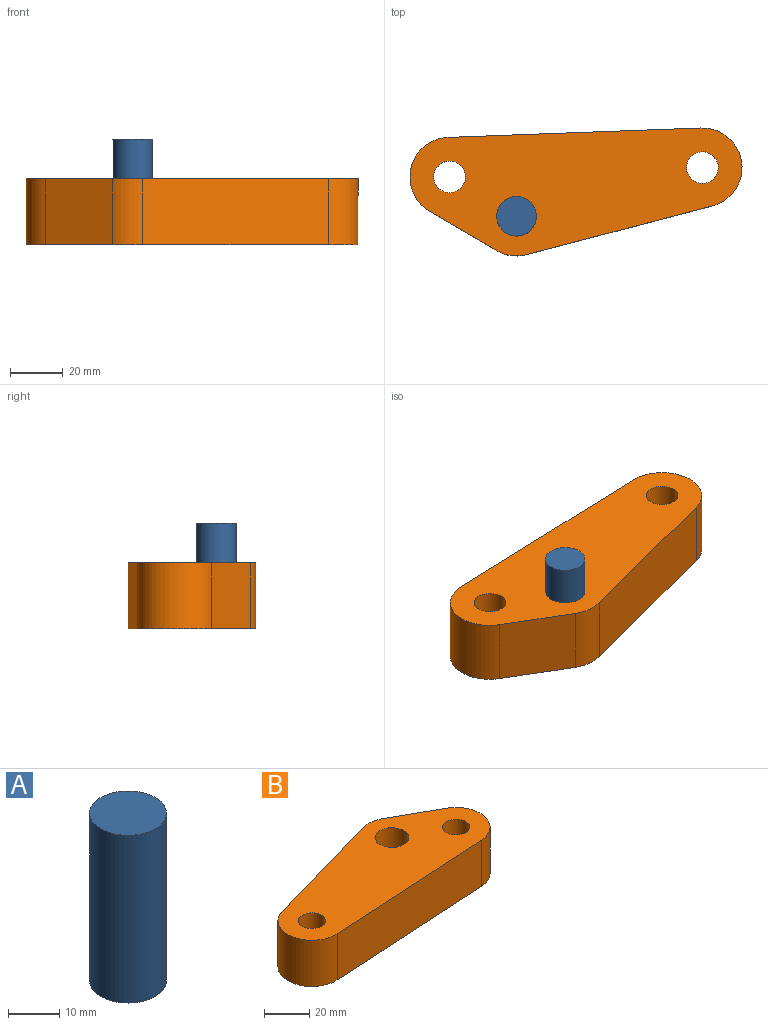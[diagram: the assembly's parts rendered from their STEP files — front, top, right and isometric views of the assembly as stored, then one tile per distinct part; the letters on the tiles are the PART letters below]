
ASSEMBLY  parts=2 mates=1
PART A: 3 faces, bbox 15x15x40 mm
  f0: cylinder r=7.5mm len=40mm, axis (0,0,-1), area 1885mm2, adj f1,f2
  f1: plane 15x15mm, normal (0,0,1), area 176.7mm2, adj f0
  f2: plane 15x15mm, normal (0,0,-1), area 176.7mm2, adj f0
PART B: 11 faces, bbox 125.7x50x25 mm
  f0: plane 70x25mm, normal (-0.27,0.96,0), area 1820mm2, adj f1,f8,f9,f10
  f1: cylinder r=15mm len=29.42mm, axis (0,0,-1), area 1096.3mm2, adj f0,f2,f9,f10
  f2: plane 95.69x25mm, normal (0.06,-1,0), area 2396.4mm2, adj f1,f3,f9,f10
  f3: cylinder r=15mm len=28.07mm, axis (0,0,-1), area 965mm2, adj f2,f4,f9,f10
  f4: plane 25.71x25mm, normal (0.49,0.87,0), area 736.2mm2, adj f3,f8,f9,f10
  f5: cylinder r=7.5mm len=25mm, axis (0,0,-1), area 1178.1mm2, adj f9,f10
  f6: cylinder r=6mm len=25mm, axis (0,0,-1), area 942.5mm2, adj f9,f10
  f7: cylinder r=6mm len=25mm, axis (0,0,-1), area 942.5mm2, adj f9,f10
  f8: cylinder r=15mm len=25mm, axis (0,0,-1), area 295.4mm2, adj f0,f4,f9,f10
  f9: plane 125.71x50mm, normal (0,0,1), area 4035.4mm2, adj f0,f1,f2,f3,f4,f5,f6,f7
  f10: plane 125.71x50mm, normal (0,0,-1), area 4035.4mm2, adj f0,f1,f2,f3,f4,f5,f6,f7
PLACE A t=(-6.81,8.65,-1.12)mm fixed
PLACE B rot(axis=(0,0,1),178.8deg) t=(-6.81,8.65,-1.12)mm
MATE revolute B.f8 <-> A.f0  axis (0,0,-1) through (-6.81,8.65,-1.12)mm
